# Revit family: Fixture_Support_Horizontal-Back-to-Back-Zurn-ZF1201-ND4-F
name_source: partatom
category: Plumbing Fixtures
units: mm (PartAtom-declared; Revit-internal decimal feet)

## family parameters
Always vertical = Yes
Cut with Voids When Loaded = No
Maintain Annotation Orientation = No
OmniClass Number = 23.45.55.11
OmniClass Title = Sanitary Components
Part Type = Normal
Room Calculation Point = No
Round Connector Dimension = Use Radius
Shared = No
Work Plane-Based = No

## types (2) — shared parameters
Assembly Code = D2030400
CW Connection = No
Coupling material = ABS - Zurn - Plastic
Description = ONE-PIECE COMBINATION BACK-TO-BACK FOOT/FACEPLATE EZCARRY® HORIZONTAL HIGH PERFORMANCE SIPHON JET NO-HUB WATER CLOSET CARRIER SYSTEM
HW Connection = No
Horizantal Pipe Diameter (Actual) = 4.5 "
Horizantal Pipe Diameter (Nominal) = 4 "
K DIM = 4.125 "
Main Material = Iron - Zurn -Cast - Painted - Blue
Manufacturer = Zurn Water, LLC
Manufacurer Brand = Zurn
Model = ZF1201-ND4-F_
Modified Date = 11/12/2025
N_Distance Bwtween Two Carriers = 13.25 "
Product Documentation Link = https://files.zurn.com
Product Installation Sheet URL = https://www.zurn.com
Product Page URL = https://www.zurn.com
Product data url = https://www.bimobject.com
Sanitary Inlet Radius = 2 "
Sanitary Outlet Radius = 2 "
Stud material = Steel-Zurn-Metal
URL = www.zurn.com
Vent Connection = Yes
Vent Connection Radius = 1 "
Vent Diameter (Actual) = 2.375 "
Vent Diameter (Nominal) = 2 "
Waste Connection = Yes
Water Closet Inlet Radius = 2 "
zero-valued in all types: CWFU, Default Elevation, HWFU, WFU

## per-type parameters (varying)
| type | Approx. Weight (Lbs) | Dim "B" | Rough_in Height |
| ZF1201-ND4-F75 | 100 | 15.875 " | 7.5 " |
| ZF1201-ND4-F55 | 93 | 13.875 " | 5.5 " |

## geometry (parser evidence)
native form markers: Sweep x12
no freeform markers — native parametric forms only
